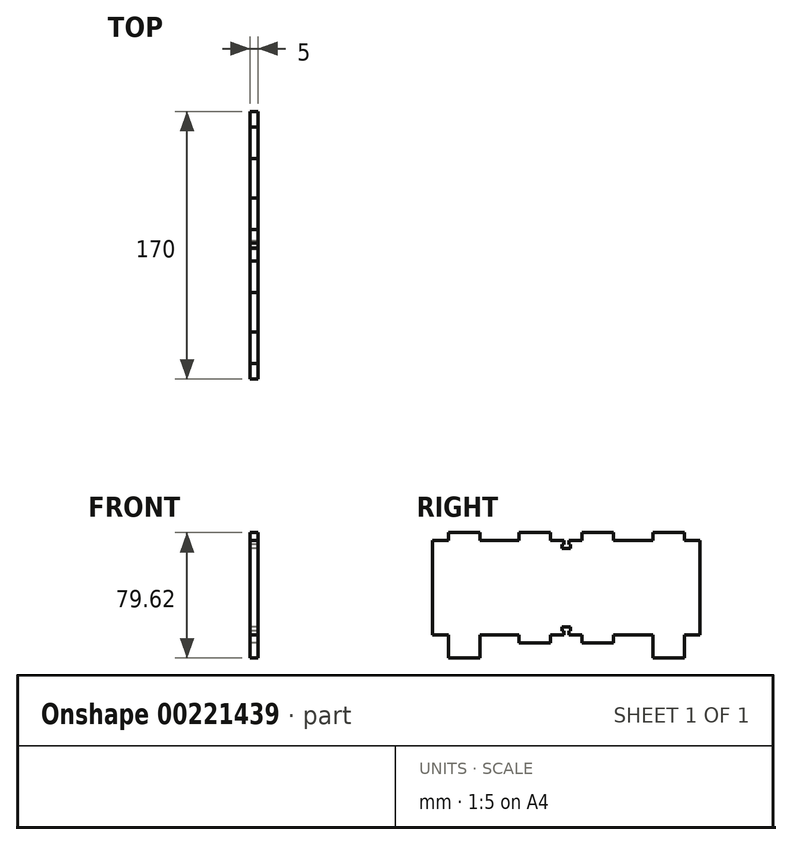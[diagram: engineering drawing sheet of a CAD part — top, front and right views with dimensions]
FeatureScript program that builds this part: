
annotation { "Feature Type Name" : "Feature", "Feature Type Description" : "" }
export const myFeature = defineFeature(function(context is Context, id is Id, definition is map)
    precondition{}
    {
        {
            assignVariable(context, id + "F0", {"name" : "thickness", "anyValue" : 5 * mm});
        }
        {
            var Q0;
            Q0=qCreatedBy(makeId("Right.planeOp"),FACE);
            var sketch = newSketch(context, id + "F1", { "sketchPlane" : qUnion([Q0])});
            skLineSegment(sketch, "E0.bottom", {"start": v(0, 0) * mm, "end": v(83.4, 0) * mm});
            skLineSegment(sketch, "E0.top", {"start": v(0, 60) * mm, "end": v(83.4, 60) * mm});
            skLineSegment(sketch, "E0.left", {"start": v(0, 0) * mm, "end": v(0, 60) * mm});
            skLineSegment(sketch, "E0.right", {"start": v(170, 0) * mm, "end": v(170, 60) * mm});
            skLineSegment(sketch, "E1", {"start": v(10, 0) * mm, "end": v(10, -14.62) * mm});
            skLineSegment(sketch, "E2", {"start": v(10, -14.62) * mm, "end": v(30, -14.62) * mm});
            skLineSegment(sketch, "E3", {"start": v(30, -14.62) * mm, "end": v(30, 0) * mm});
            skLineSegment(sketch, "E4", {"start": v(55, 0) * mm, "end": v(55, -5) * mm});
            skLineSegment(sketch, "E5", {"start": v(55, -5) * mm, "end": v(75, -5) * mm});
            skLineSegment(sketch, "E6", {"start": v(75, -5) * mm, "end": v(75, 0) * mm});
            skLineSegment(sketch, "E7", {"start": v(85, 60) * mm, "end": v(85, 0) * mm, "construction": true});
            skLineSegment(sketch, "E8.MirrorCS", {"start": v(95, -5) * mm, "end": v(95, 0) * mm});
            skLineSegment(sketch, "E9.MirrorCS", {"start": v(115, -5) * mm, "end": v(95, -5) * mm});
            skLineSegment(sketch, "E10.MirrorCS", {"start": v(115, 0) * mm, "end": v(115, -5) * mm});
            skLineSegment(sketch, "E11.MirrorCS", {"start": v(140, -14.62) * mm, "end": v(140, 0) * mm});
            skLineSegment(sketch, "E12.MirrorCS", {"start": v(160, -14.62) * mm, "end": v(140, -14.62) * mm});
            skLineSegment(sketch, "E13.MirrorCS", {"start": v(160, 0) * mm, "end": v(160, -14.62) * mm});
            skLineSegment(sketch, "E14", {"start": v(83.4, 0) * mm, "end": v(83.4, 2.5) * mm});
            skLineSegment(sketch, "E15", {"start": v(83.4, 2.5) * mm, "end": v(82.25, 2.5) * mm});
            skLineSegment(sketch, "E16", {"start": v(82.25, 2.5) * mm, "end": v(82.25, 5) * mm});
            skLineSegment(sketch, "E17", {"start": v(82.25, 5) * mm, "end": v(85, 5) * mm});
            skLineSegment(sketch, "E18.MirrorCS", {"start": v(86.6, 2.5) * mm, "end": v(87.75, 2.5) * mm});
            skLineSegment(sketch, "E19.MirrorCS", {"start": v(87.75, 5) * mm, "end": v(85, 5) * mm});
            skLineSegment(sketch, "E20.MirrorCS", {"start": v(87.75, 2.5) * mm, "end": v(87.75, 5) * mm});
            skLineSegment(sketch, "E21.MirrorCS", {"start": v(86.6, 0) * mm, "end": v(86.6, 2.5) * mm});
            skLineSegment(sketch, "E22", {"start": v(0, 30) * mm, "end": v(170, 30) * mm, "construction": true});
            skLineSegment(sketch, "E23.MirrorCS", {"start": v(83.4, 57.5) * mm, "end": v(82.25, 57.5) * mm});
            skLineSegment(sketch, "E24.MirrorCS", {"start": v(87.75, 57.5) * mm, "end": v(87.75, 55) * mm});
            skLineSegment(sketch, "E25.MirrorCS", {"start": v(86.6, 60) * mm, "end": v(86.6, 57.5) * mm});
            skLineSegment(sketch, "E26.MirrorCS", {"start": v(86.6, 57.5) * mm, "end": v(87.75, 57.5) * mm});
            skLineSegment(sketch, "E27.MirrorCS", {"start": v(82.25, 57.5) * mm, "end": v(82.25, 55) * mm});
            skLineSegment(sketch, "E28.MirrorCS", {"start": v(83.4, 60) * mm, "end": v(83.4, 57.5) * mm});
            skLineSegment(sketch, "E29.MirrorCS", {"start": v(82.25, 55) * mm, "end": v(85, 55) * mm});
            skLineSegment(sketch, "E30.MirrorCS", {"start": v(87.75, 55) * mm, "end": v(85, 55) * mm});
            skLineSegment(sketch, "E31.MirrorCS", {"start": v(95, 65) * mm, "end": v(95, 60) * mm});
            skLineSegment(sketch, "E32.MirrorCS", {"start": v(75, 65) * mm, "end": v(75, 60) * mm});
            skLineSegment(sketch, "E33.MirrorCS", {"start": v(55, 60) * mm, "end": v(55, 65) * mm});
            skLineSegment(sketch, "E34.MirrorCS", {"start": v(115, 60) * mm, "end": v(115, 65) * mm});
            skLineSegment(sketch, "E35.MirrorCS", {"start": v(115, 65) * mm, "end": v(95, 65) * mm});
            skLineSegment(sketch, "E36.MirrorCS", {"start": v(55, 65) * mm, "end": v(75, 65) * mm});
            skLineSegment(sketch, "E37", {"start": v(10, 60) * mm, "end": v(10, 65) * mm});
            skLineSegment(sketch, "E38", {"start": v(10, 65) * mm, "end": v(30, 65) * mm});
            skLineSegment(sketch, "E39", {"start": v(30, 65) * mm, "end": v(30, 60) * mm});
            skLineSegment(sketch, "E40.MirrorCS", {"start": v(140, 65) * mm, "end": v(140, 60) * mm});
            skLineSegment(sketch, "E41.MirrorCS", {"start": v(160, 60) * mm, "end": v(160, 65) * mm});
            skLineSegment(sketch, "E42.MirrorCS", {"start": v(160, 65) * mm, "end": v(140, 65) * mm});
            skLineSegment(sketch, "E43.trimOffspring", {"start": v(86.6, 0) * mm, "end": v(170, 0) * mm});
            skLineSegment(sketch, "E44.trimOffspring", {"start": v(86.6, 60) * mm, "end": v(170, 60) * mm});
            skSolve(sketch);
        }
        {
            var Q0;
            Q0=qSketchRegion(id+"F1",true);
            extrude(context, id + "F2", {"entities" : qUnion([Q0]), "depth" : getVariable(context, 'thickness')});
        }
    });
